# Revit family: a_reynaers_cs-77-functional_door_inside-opening-brush_singlerfa
name_source: partatom
category: Windows
revit_build: Autodesk Revit 2017 (Build: 20160225_1515(x64)
units: mm (PartAtom-declared; Revit-internal decimal feet)

## family parameters
Always vertical = Yes
Cut with Voids When Loaded = No
Host = Wall
OmniClass Number = 23.30.20.00
OmniClass Title = Windows
Room Calculation Point = No
Shared = No

## types (2) — shared parameters
Analytic Construction = <None>
BE = No
Date of publishing = 2015-09-17
Design country = Belgium
Edition number = 1
IFC Classification = Window
Manufacturer = Reynaers
Manufacturer country = Belgium
Manufacturer name = Reynaers
Material main = Aluminium
Material secondary = Aluminium
NBS Reference Code = 59-97
NBS Reference Description = Windows
NL = Yes
Product Guid = 9fe012cc-205e-434f-a607-7c1aed2f5c3e
Product SKU = Reynaers_window_Concept_system_77
Product family = Windows & Doors
Product group = Windows Aluminium
REY Block Frame = No
REY Brush Profile Height = 26 mm
REY Built-In Depth = 68 mm
REY Butt Strip Width = 25 mm  [stored 0.082021 ft]
REY Fixation Bottom = 33 mm  [stored 0.108268 ft]
REY Gap Floor = 13 mm
REY Gap Width = 6 mm  [stored 0.019685 ft]
REY Joint Width = 8 mm  [stored 0.0262467 ft]
REY Joint Width A = 8 mm  [stored 0.0262467 ft]
REY Offset Wall Ext Int = 25 mm  [stored 0.082021 ft]
REY Offset Wall Ext Int A = 25 mm  [stored 0.082021 ft]
REY Panel Coverage = 19 mm  [stored 0.062336 ft]
REY Profile Rebate = 25 mm  [stored 0.082021 ft]
REY Rebate = 30 mm  [stored 0.0984252 ft]
REY Rebate A = 30 mm  [stored 0.0984252 ft]
REY Rebate TOP A = 30 mm  [stored 0.0984252 ft]
REY Shutter = No
REY Shutter Position = 25 mm  [stored 0.082021 ft]
REY Shutter Roll Height = 200 mm  [stored 0.656168 ft]
REY Shutter Roll Material = <By Category>
REY Vent Width = 76 mm  [stored 0.249344 ft]
REY Website = www.reynaers.com
UNSPSC Code = 301716
URL = http://www.reynaers.com
Uniclass 1.4 Code = JL10
Uniclass 1.4 Description = Windows
Uniclass 2.0 Code = PR-59-97
Uniclass 2.0 Description = Windows
Wall Closure = By host
Wall Exterior Width = 90 mm  [stored 0.295276 ft]
zero-valued in all types: Default Sill Height, Nominal height, Nominal width, REY Design, REY Joint Bottom, REY Joint Width B, REY Offset Wall Ext Int B, REY Rebate B, REY Rebate TOP B, REY Shutter Depth, REY Shutter Height, REY Sill H, REY Sill Height, Weight Net (Kg)

## per-type parameters (varying)
| type | Product data url | QR code | REY Frame Width |
| Frame 68mm | http://bimobject.com | http://bimobject.com | 68 mm |
| Frame 77mm | http://file-system.ru | http://file-system.ru | 77 mm  [stored 0.252625 ft] |

note: [stored X ft] marks values corroborated as IEEE doubles in the binary element streams (Revit-internal decimal feet)

## geometry (parser evidence)
native form markers: Sweep x4
no freeform markers — native parametric forms only
